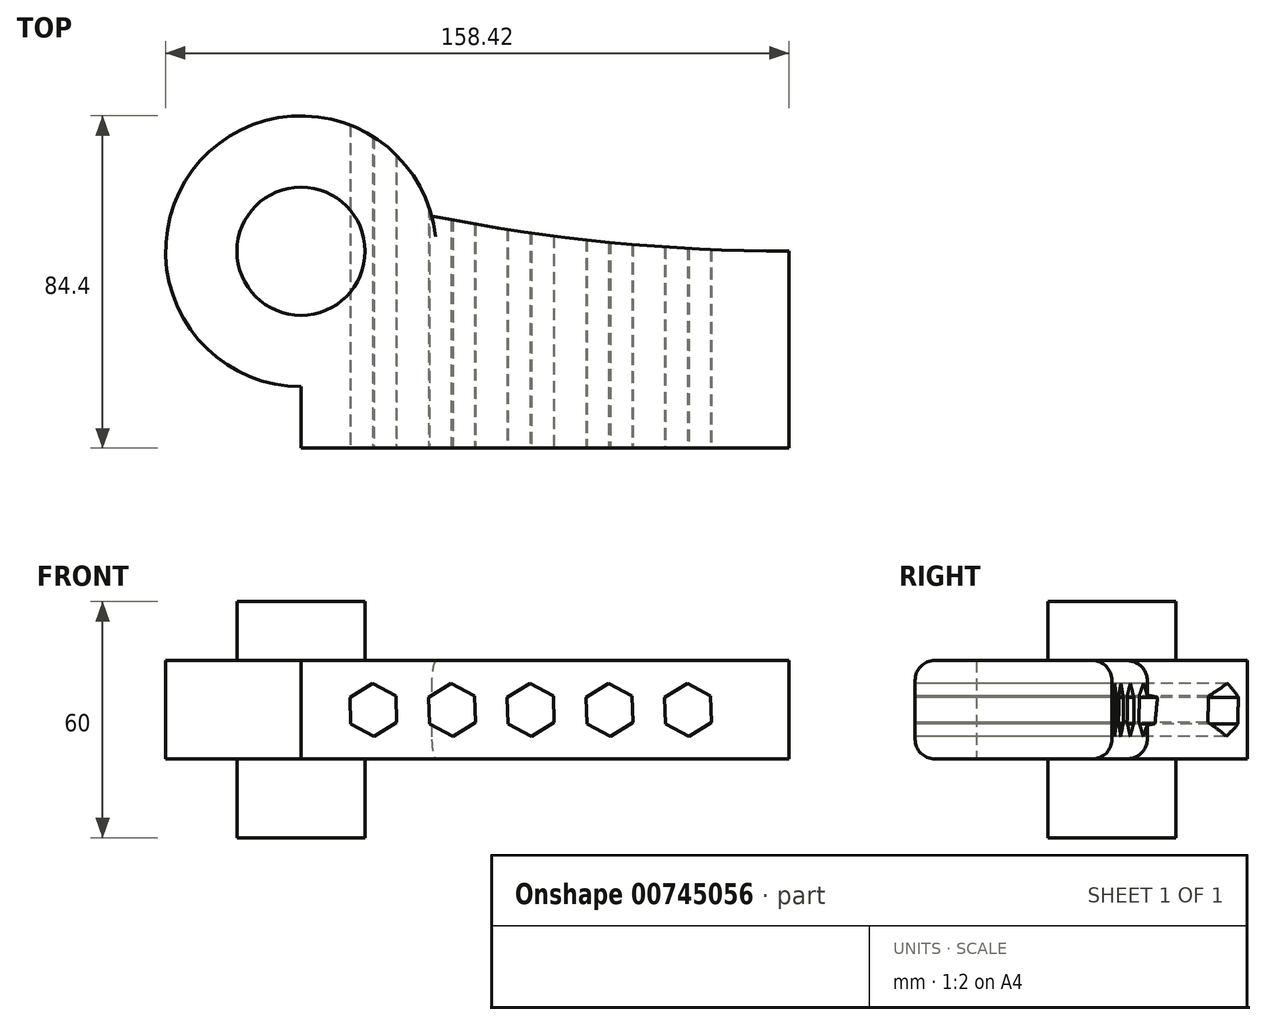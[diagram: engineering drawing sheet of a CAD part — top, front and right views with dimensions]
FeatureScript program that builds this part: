
annotation { "Feature Type Name" : "Feature", "Feature Type Description" : "" }
export const myFeature = defineFeature(function(context is Context, id is Id, definition is map)
    precondition{}
    {
        {
            var Q0;
            Q0=qCreatedBy(makeId("Top.planeOp"),FACE);
            var sketch = newSketch(context, id + "F0", { "sketchPlane" : qUnion([Q0])});
            skLineSegment(sketch, "E0.bottom", {"start": v(62.01, -25) * mm, "end": v(-62.01, -25) * mm});
            skLineSegment(sketch, "E0.top", {"start": v(62.01, 25) * mm, "end": v(-62.01, 25) * mm});
            skLineSegment(sketch, "E0.left", {"start": v(62.01, -25) * mm, "end": v(62.01, 25) * mm});
            skLineSegment(sketch, "E0.right", {"start": v(-62.01, -25) * mm, "end": v(-62.01, 25) * mm});
            skPoint(sketch, "E0.middle", {"position": v(0, 0) * mm});
            skCircle(sketch, "E1", {"center": v(-62.01, 25) * mm, "radius": 16.28 * mm});
            skCircle(sketch, "E2", {"center": v(-62.01, 25) * mm, "radius": 34.4 * mm});
            skArc(sketch, "E3", {"start": v(-57.8, 40.73) * mm, "mid": v(1.59, 28.95) * mm, "end": v(62.01, 25) * mm});
            skSolve(sketch);
        }
        {
            var Q0;
            Q0 = qSketchRegion(id + "F0", true);
            extrude(context, id + "F1", {"entities" : qUnion([Q0]), "depth" : 25 * mm, "offsetDistance" : 25 * mm});
        }
        {
            var Q0;
            {var subQ0=sQuery(id+"F0.wireOp",EDGE,"E0.right");var subQ1=sQuery(id+"F0.wireOp",EDGE,"E0.top");var subQ2=makeQuery(id+"F0.imprint","INTERSECT",VERTEX,{"derivedFrom":[subQ1,subQ0]});Q0=makeQuery(id+"F0.imprint","IMPRINT",FACE,{"disambiguationData":[TD([[makeQuery(id+"F0.imprint","IMPRINT",EDGE,{"disambiguationData":[TD([[subQ2,1.0]])],"derivedFrom":subQ1}),-1.0]])]});}
            var Q1;
            {var subQ0=sQuery(id+"F0.wireOp",EDGE,"E0.right");var subQ1=sQuery(id+"F0.wireOp",EDGE,"E0.top");var subQ2=makeQuery(id+"F0.imprint","INTERSECT",VERTEX,{"derivedFrom":[subQ1,subQ0]});Q1=makeQuery(id+"F0.imprint","IMPRINT",FACE,{"disambiguationData":[TD([[makeQuery(id+"F0.imprint","IMPRINT",EDGE,{"disambiguationData":[TD([[subQ2,1.0]])],"derivedFrom":subQ1}),1.0]])]});}
            extrude(context, id + "F2", {"entities" : qUnion([Q0, Q1]), "operationType" : NewBodyOperationType.ADD, "depth" : 40 * mm, "offsetDistance" : 25 * mm, "hasSecondDirection" : true, "secondDirectionOppositeDirection" : true, "secondDirectionDepth" : 20 * mm});
        }
        {
            var Q0;
            Q0=makeQuery(id+"F1.opExtrude","SWEPT_FACE",FACE,{"disambiguationData":[OSD([sQuery(id+"F0.wireOp",EDGE,"E0.bottom")])]});
            var sketch = newSketch(context, id + "F3", { "sketchPlane" : qUnion([Q0])});
            skCircle(sketch, "E4.cCircle", {"center": v(-43.66, 12.5) * mm, "radius": 5.85 * mm, "construction": true});
            skPoint(sketch, "E4.cCircle.centerSnap0", {"position": v(-62.01, 12.5) * mm});
            skLineSegment(sketch, "E4.0", {"start": v(-37.7, 9.32) * mm, "end": v(-43.43, 5.75) * mm});
            skLineSegment(sketch, "E4.1", {"start": v(-43.43, 5.75) * mm, "end": v(-49.39, 8.93) * mm});
            skLineSegment(sketch, "E4.2", {"start": v(-49.39, 8.93) * mm, "end": v(-49.61, 15.68) * mm});
            skLineSegment(sketch, "E4.3", {"start": v(-49.61, 15.68) * mm, "end": v(-43.88, 19.25) * mm});
            skLineSegment(sketch, "E4.4", {"start": v(-43.88, 19.25) * mm, "end": v(-37.93, 16.07) * mm});
            skLineSegment(sketch, "E4.5", {"start": v(-37.93, 16.07) * mm, "end": v(-37.7, 9.32) * mm});
            skPoint(sketch, "E4.0.midPoint", {"position": v(-40.56, 7.54) * mm});
            skLineSegment(sketch, "E5.1.0.0", {"start": v(-29.61, 15.68) * mm, "end": v(-23.88, 19.25) * mm});
            skLineSegment(sketch, "E5.1.0.1", {"start": v(-29.39, 8.93) * mm, "end": v(-29.61, 15.68) * mm});
            skLineSegment(sketch, "E5.1.0.2", {"start": v(-23.43, 5.75) * mm, "end": v(-29.39, 8.93) * mm});
            skLineSegment(sketch, "E5.1.0.3", {"start": v(-17.7, 9.32) * mm, "end": v(-23.43, 5.75) * mm});
            skLineSegment(sketch, "E5.1.0.4", {"start": v(-17.93, 16.07) * mm, "end": v(-17.7, 9.32) * mm});
            skLineSegment(sketch, "E5.1.0.5", {"start": v(-23.88, 19.25) * mm, "end": v(-17.93, 16.07) * mm});
            skLineSegment(sketch, "E5.2.0.0", {"start": v(-9.61, 15.68) * mm, "end": v(-3.88, 19.25) * mm});
            skLineSegment(sketch, "E5.2.0.1", {"start": v(-9.39, 8.93) * mm, "end": v(-9.61, 15.68) * mm});
            skLineSegment(sketch, "E5.2.0.2", {"start": v(-3.43, 5.75) * mm, "end": v(-9.39, 8.93) * mm});
            skLineSegment(sketch, "E5.2.0.3", {"start": v(2.3, 9.32) * mm, "end": v(-3.43, 5.75) * mm});
            skLineSegment(sketch, "E5.2.0.4", {"start": v(2.07, 16.07) * mm, "end": v(2.3, 9.32) * mm});
            skLineSegment(sketch, "E5.2.0.5", {"start": v(-3.88, 19.25) * mm, "end": v(2.07, 16.07) * mm});
            skLineSegment(sketch, "E5.3.0.0", {"start": v(10.39, 15.68) * mm, "end": v(16.12, 19.25) * mm});
            skLineSegment(sketch, "E5.3.0.1", {"start": v(10.61, 8.93) * mm, "end": v(10.39, 15.68) * mm});
            skLineSegment(sketch, "E5.3.0.2", {"start": v(16.57, 5.75) * mm, "end": v(10.61, 8.93) * mm});
            skLineSegment(sketch, "E5.3.0.3", {"start": v(22.3, 9.32) * mm, "end": v(16.57, 5.75) * mm});
            skLineSegment(sketch, "E5.3.0.4", {"start": v(22.07, 16.07) * mm, "end": v(22.3, 9.32) * mm});
            skLineSegment(sketch, "E5.3.0.5", {"start": v(16.12, 19.25) * mm, "end": v(22.07, 16.07) * mm});
            skLineSegment(sketch, "E5.4.0.0", {"start": v(30.39, 15.68) * mm, "end": v(36.12, 19.25) * mm});
            skLineSegment(sketch, "E5.4.0.1", {"start": v(30.61, 8.93) * mm, "end": v(30.39, 15.68) * mm});
            skLineSegment(sketch, "E5.4.0.2", {"start": v(36.57, 5.75) * mm, "end": v(30.61, 8.93) * mm});
            skLineSegment(sketch, "E5.4.0.3", {"start": v(42.3, 9.32) * mm, "end": v(36.57, 5.75) * mm});
            skLineSegment(sketch, "E5.4.0.4", {"start": v(42.07, 16.07) * mm, "end": v(42.3, 9.32) * mm});
            skLineSegment(sketch, "E5.4.0.5", {"start": v(36.12, 19.25) * mm, "end": v(42.07, 16.07) * mm});
            skLineSegment(sketch, "E5.direction1", {"start": v(-49.39, 8.93) * mm, "end": v(-29.39, 8.93) * mm, "construction": true});
            skSolve(sketch);
        }
        {
            var Q0;
            Q0=makeQuery(id+"F3.imprint","IMPRINT",FACE,{"disambiguationData":[TD([[makeQuery(id+"F3.imprint","IMPRINT",EDGE,{"derivedFrom":sQuery(id+"F3.wireOp",EDGE,"E4.0")}),-1.0]])]});
            var Q1;
            Q1=makeQuery(id+"F3.imprint","IMPRINT",FACE,{"disambiguationData":[TD([[makeQuery(id+"F3.imprint","IMPRINT",EDGE,{"derivedFrom":sQuery(id+"F3.wireOp",EDGE,"E5.1.0.0")}),-1.0]])]});
            var Q2;
            Q2=makeQuery(id+"F3.imprint","IMPRINT",FACE,{"disambiguationData":[TD([[makeQuery(id+"F3.imprint","IMPRINT",EDGE,{"derivedFrom":sQuery(id+"F3.wireOp",EDGE,"E5.2.0.0")}),-1.0]])]});
            var Q3;
            Q3=makeQuery(id+"F3.imprint","IMPRINT",FACE,{"disambiguationData":[TD([[makeQuery(id+"F3.imprint","IMPRINT",EDGE,{"derivedFrom":sQuery(id+"F3.wireOp",EDGE,"E5.3.0.0")}),-1.0]])]});
            var Q4;
            Q4=makeQuery(id+"F3.imprint","IMPRINT",FACE,{"disambiguationData":[TD([[makeQuery(id+"F3.imprint","IMPRINT",EDGE,{"derivedFrom":sQuery(id+"F3.wireOp",EDGE,"E5.4.0.0")}),-1.0]])]});
            extrude(context, id + "F4", {"entities" : qUnion([Q0, Q1, Q2, Q3, Q4]), "operationType" : NewBodyOperationType.REMOVE, "endBound" : BoundingType.THROUGH_ALL, "oppositeDirection" : true, "depth" : 25 * mm, "offsetDistance" : 25 * mm});
        }
        {
            var Q0;
            Q0=makeQuery(id+"F1.opExtrude","CAP_EDGE",EDGE,{"disambiguationData":[OSD([sQuery(id+"F0.wireOp",EDGE,"E0.bottom")])],"isStart":false});
            var Q1;
            Q1=makeQuery(id+"F1.opExtrude","CAP_EDGE",EDGE,{"disambiguationData":[OSD([sQuery(id+"F0.wireOp",EDGE,"E0.bottom")])],"isStart":true});
            var Q2;
            Q2=makeQuery(id+"F1.opExtrude","CAP_EDGE",EDGE,{"disambiguationData":[OSD([sQuery(id+"F0.wireOp",EDGE,"E3")])],"isStart":true});
            var Q3;
            Q3=makeQuery(id+"F1.opExtrude","CAP_EDGE",EDGE,{"disambiguationData":[OSD([sQuery(id+"F0.wireOp",EDGE,"E3")])],"isStart":false});
            fillet(context, id + "F5", {"entities" : qUnion([Q0, Q1, Q2, Q3]), "radius" : 5 * mm, "tangentPropagation" : true, "allowEdgeOverflow" : false});
        }
    });
